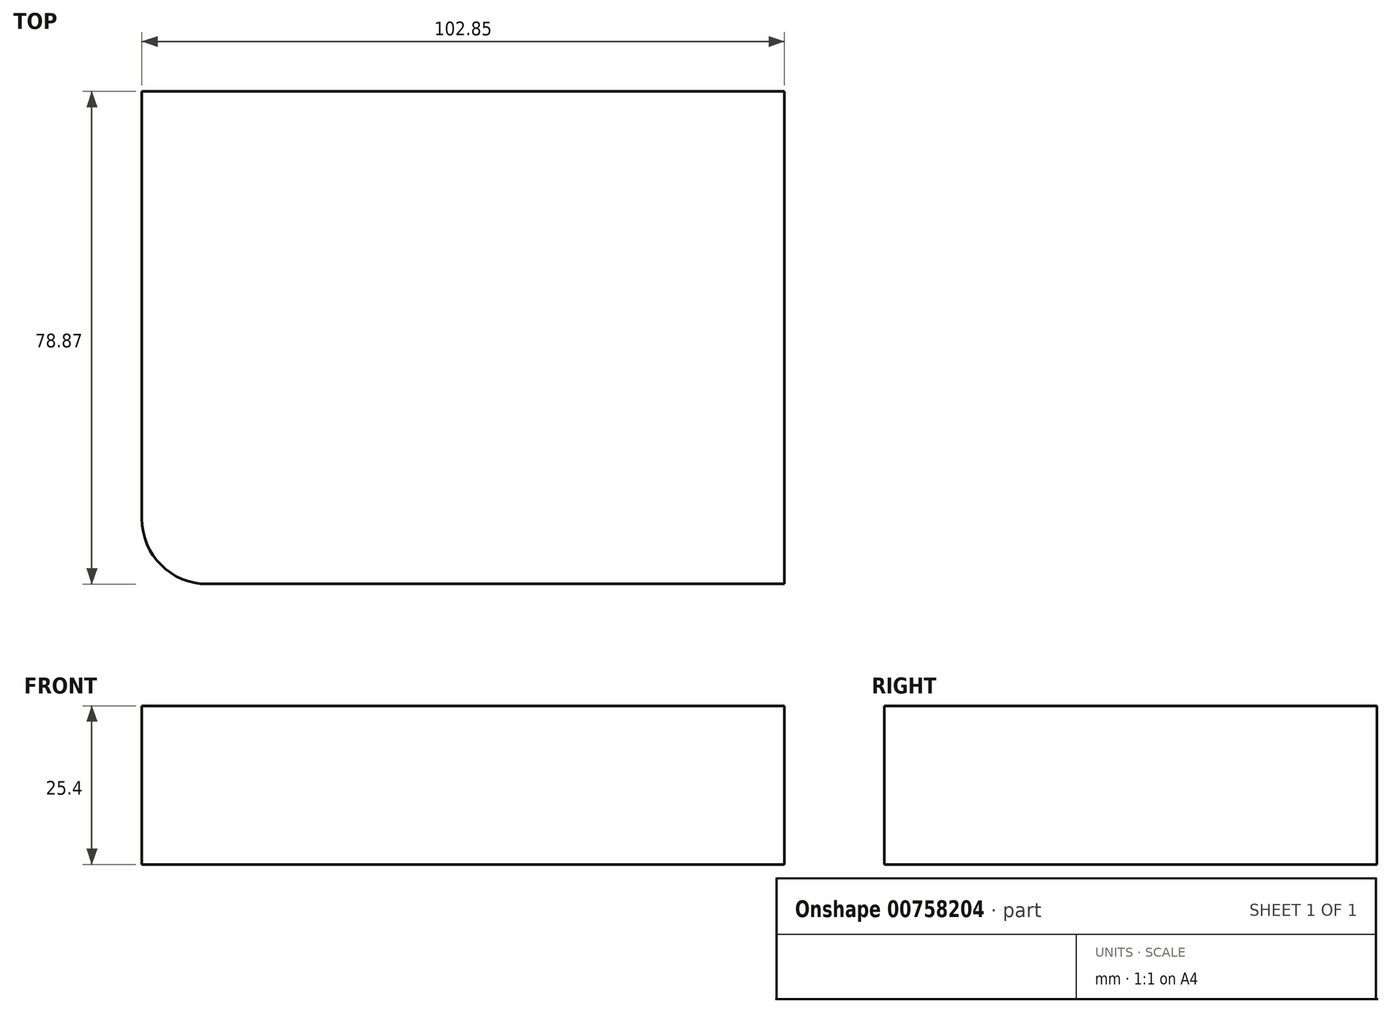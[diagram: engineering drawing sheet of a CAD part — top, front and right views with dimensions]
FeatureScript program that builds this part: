
annotation { "Feature Type Name" : "Feature", "Feature Type Description" : "" }
export const myFeature = defineFeature(function(context is Context, id is Id, definition is map)
    precondition{}
    {
        {
            var Q0;
            Q0=qCreatedBy(makeId("Top.planeOp"),FACE);
            var sketch = newSketch(context, id + "F0", { "sketchPlane" : qUnion([Q0])});
            skLineSegment(sketch, "E0.bottom", {"start": v(-54.87, 41.52) * mm, "end": v(47.98, 41.52) * mm});
            skLineSegment(sketch, "E0.top", {"start": v(-54.87, -37.35) * mm, "end": v(47.98, -37.35) * mm});
            skLineSegment(sketch, "E0.left", {"start": v(-54.87, 41.52) * mm, "end": v(-54.87, -37.35) * mm});
            skLineSegment(sketch, "E0.right", {"start": v(47.98, 41.52) * mm, "end": v(47.98, -37.35) * mm});
            skSolve(sketch);
        }
        {
            var Q0;
            Q0 = qSketchRegion(id + "F0", true);
            extrude(context, id + "F1", {"entities" : qUnion([Q0]), "depth" : 25.4 * mm, "offsetDistance" : 25.4 * mm});
        }
        {
            var Q0;
            Q0=makeQuery(id+"F1.opExtrude","SWEPT_EDGE",EDGE,{"disambiguationData":[OSD([sQuery(id+"F0.wireOp",EDGE,"E0.top"),sQuery(id+"F0.wireOp",EDGE,"E0.left")])]});
            fillet(context, id + "F2", {"entities" : qUnion([Q0]), "radius" : 10.42 * mm, "allowEdgeOverflow" : false});
        }
    });
